# Revit family: MHY-15
name_source: partatom
category: Plumbing Fixtures
units: mm (PartAtom-declared; Revit-internal decimal feet)

## family parameters
Classification Number = 23.45.55.21
Cut with Voids When Loaded = No
Enable Cutting in Views = No
Host = Face
Maintain Annotation Orientation = No
Part Type = Normal
Room Calculation Point = No
Round Connector Dimension = Use Diameter
Shared = No

## types (14) — shared parameters
Description = Non-Freeze Wall Hydrant
Hydrant Material = Chrome Plated
Manufacturer = MIFAB
Model = MHY-15
URL = www.mifab.com
zero-valued in all types: Default Elevation, WFU

## per-type parameters (varying)
| type | Wall Thikness |
| MHY-15-4 | 4 " |
| MHY-15-6 | 6 " |
| MHY-15-8 | 8 " |
| MHY-15-10 | 10 " |
| MHY-15-12 | 12 " |
| MHY-15-14 | 14 " |
| MHY-15-16 | 16 " |
| MHY-15-18 | 18 " |
| MHY-15-20 | 20 " |
| MHY-15-22 | 22 " |
| MHY-15-24 | 24 " |
| MHY-15-26 | 26 " |
| MHY-15-28 | 28 " |
| MHY-15-30 | 30 " |

## geometry (parser evidence)
native form markers: Blend x3, Sweep x3
no freeform markers — native parametric forms only
